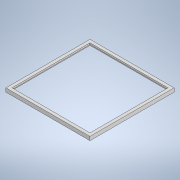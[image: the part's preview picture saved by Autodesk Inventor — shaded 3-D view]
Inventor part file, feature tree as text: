
AUTODESK INVENTOR PART (.ipt)
format: ipt  version: 2020.2 (Build 242310000, 310)  size: 123,904 bytes
history: native  units: mm
features: extrude x2, sketch x2, projected_geometry x1
ambient origin geometry x8: Origin, YZ Plane, XZ Plane, XY Plane, X Axis, Y Axis, Z Axis, Center Point
bodies: Solid1 (feature_tree)
feature tree (5):
  extrude  "Extrusion1"  Depth=2.0mm TaperAngle=0.0deg
  extrude  "Extrusion2"  Depth=2.0mm
  sketch  "Sketch1"  dims[d0=108.004mm d4=2.0mm d5=0.0mm]
  sketch  "Sketch2"  dims[d7=3.0mm d8=0.0mm d9=0.1mm d10=2.0mm d11=2.0mm d12=2.0mm]
  projected_geometry  "Projected Loop1"
